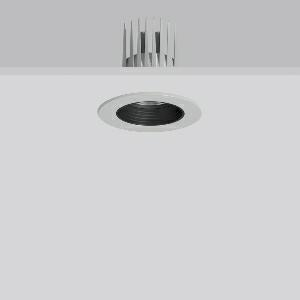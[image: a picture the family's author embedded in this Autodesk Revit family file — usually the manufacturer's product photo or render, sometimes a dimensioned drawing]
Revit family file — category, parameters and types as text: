
# Revit family: heledon_mini_e_901752_004_76_37c8
name_source: partatom
category: Lighting Fixtures
units: mm (PartAtom-declared; Revit-internal decimal feet)

## family parameters
Cut with Voids When Loaded = No
Host = Face
Light Source = No
Part Type = Normal
Room Calculation Point = No
Round Connector Dimension = Use Diameter
Shared = No

## types (1)
- HELEDON mini E (1 x LED Modul 930, 3000 lm, 3000)
    Apparent Load = 29 VA
    Approval mark = CE
    CIE Flux Codes = 96 100 100 100 100
    Color Rendering = 90
    Color Temperature = 3000
    Default Elevation = 1800 mm
    Description = Series: HELEDON mini
Round recessed downlight. Housing: die-cast aluminium, powder-coated. Black plastic ring and recessed LED to prevent glare from the side. Optical assembly with lens made of plastic (polycarbonate) for the best homogeneous light distribution - can be changed without tools. Best colour rendering index Ra>90. Suitable for Recessed ceiling mounting. Installation without tools thanks to spring fastening system. Including separate LED converter with connecting cable 600 mm.High quality converter without flickering and stroboscopic effect. Through-wiring box (5 pole) available as accessory. The following accessories can be mounted without use of tools: interchangeable lenses, decorative glasses, honeycomb louvre, clear and frosted diffusers, white interchangeable plastic ring. 
Colour: silver
Diameter: 124 mm
Height: 3 mm
Cut-out diameter: 114 mm
Recess height: 170 mm
Luminaire: recess height: 120 mm
Lamp: LED
Socket: without socket
Colour temperature: 3000K
Colour rendering index (CRI): 92
System power: 29 W
Rated luminous flux: 3000 lm
Luminous efficiency: 103 lm/W
Control gear: Converter, dimmable, DALI
Protection class: II
Type of protection: IP 20
    Height = 0 mm  [stored 0 ft]
    Lamp = 1 x LED Modul 930
    Lamp Light Flux = 3000 lm
    Lamp count = 1
    Length = 124 mm  [stored 0.406824 ft]
    Lifetime = 50000 h
    Luminous efficacy = 103 lm/W
    Manufacturer = RZB
    ModVariant = No
    Model = 901752.004.76
    Mounting Place = Ceiling
    Mounting Type = Recessed
    Number of Poles = 1
    OnlyDefault = Yes
    Power Factor = 1
    Product Name = HELEDON mini E
    Product group = Recessed downlights
    ProductGroupID = 402
    Protection Class = Protection class II
    Protection Degree = IP 20
    RLX_Detail_Level = 1
    RLX_Emergency_Light_Flux = 0 lm
    RLX_Emergency_Type = 0
    RLX_Emergency_Type_DB = No
    RlxData = <blob elided: 128213 chars, md5=479ee31e>
    Socket = socket
    Standby Power = 0 W
    System Light Flux = 3000 lm
    System Power = 29 W
    Type Comments = Product without accessories
    Type Image = 901656.004.jpg
    URL = http://relux.com
    VarID = ---
    Voltage = 230 V
    Voltage Range = 220-240 V
    Weight = 0.00 kg
    Width = 0 mm  [stored 0 ft]

note: [stored X ft] marks values corroborated as IEEE doubles in the binary element streams (Revit-internal decimal feet)

## geometry (parser evidence)
native form markers: Blend x4, Sweep x13
no freeform markers — native parametric forms only
